# Revit family: Hager-Golf-IP40-Plain_Door-syst-CH-fr
name_source: partatom
category: Electrical Equipment
units: mm (PartAtom-declared; Revit-internal decimal feet)

## family parameters
Cut with Voids When Loaded = No
Host = Face
Panel Configuration = Two Columns, Circuits Across
Part Type = Panelboard
Room Calculation Point = No
Round Connector Dimension = Use Diameter
Shared = No

## types (22) — shared parameters
EF000007 - couleur = EV000202 - blanc
EF000116 - numéro RAL = 9010
EF000118 - avec cadre/support de montage = No
EF000339 - type de capot = EV004216 - porte
EF001062 - finition CEM = No
EF001088 - possibilité de montage en saillie = Yes
EF001596 - matériau du boîtier/corps = EV000139 - plastique
EF004462 - type de fermeture = EV000154 - autre
EF006244 - couvercle/porte transparent(e) = No
EF006306 - avec serrure = No
EF009212 - finition du couvercle = EV000116 - fermé
EF015941 - porte pour transmission du signal = Yes
HG000001 - nombre de colonnes = 1
HG000002 - avec porte = Yes
HG000003 - Gamme = Golf
HG000005 - Epaisseur = 3 mm  [stored 0.00984252 ft]
HG000009 - Porte à double battant = No
HG000010 - Portes asymétriques = No
HG000011 - Rangées du bas vides = No
HG000017 - Distance entre pôles = 18 mm  [stored 0.0590551 ft]
Manufacturer = Hager
Type Comments = Golf
zero-valued in all types: Default Elevation, HG000007 - Nombre de colonnes vides, HG000008 - Nombre de rangées vides

## per-type parameters (varying)
| type | EF000003 - mode de pose | EF000008 - largeur | EF000040 - hauteur | EF000049 - profondeur | EF000218 - profondeur d'encastrement | EF000266 - nombre de rangées | EF000332 - hauteur d'encastrement | EF000846 - largeur d'encastrement | EF001131 - profondeur intérieure | EF001134 - rail DIN | EF002950 - largeur en nombre de modules | EF005474 - indice de protection (IP) | EF015776 - borne de mise à la terre | EF015777 - borne à conducteur neutre | HG000004 - Référence fabricant | HG000006 - Encastré | Model |
| Encastré  L204 H225 P97.5 4 Modules - VF104PS | EV000383 - encastré | 204 mm | 225 mm  [stored 0.738189 ft] | 98 mm  [stored 0.321522 ft] | 72 mm  [stored 0.23622 ft] | 1 | 189 mm  [stored 0.620079 ft] | 170 mm  [stored 0.557743 ft] | 98 mm  [stored 0.321522 ft] | Yes | 4 |  | No | No | VF104PS | Yes | VF104PS |
| Encastré  L275 H225 P97.5 8 Modules - VF108PS | EV000383 - encastré | 275 mm | 225 mm  [stored 0.738189 ft] | 98 mm  [stored 0.321522 ft] | 72 mm  [stored 0.23622 ft] | 1 | 189 mm  [stored 0.620079 ft] | 242 mm  [stored 0.793963 ft] | 98 mm  [stored 0.321522 ft] | Yes | 8 |  | No | No | VF108PS | Yes | VF108PS |
| Encastré IP40 L352 H293 P97.5 12 Modules - VF112PS | EV000383 - encastré | 352 mm  [stored 1.15486 ft] | 293 mm | 98 mm  [stored 0.321522 ft] | 72 mm  [stored 0.23622 ft] | 1 | 257 mm  [stored 0.843176 ft] | 318 mm  [stored 1.04331 ft] | 98 mm  [stored 0.321522 ft] | Yes | 12 | EV006415 - IP40 | Yes | Yes | VF112PS | Yes | VF112PS |
| Encastré IP40 L352 H543 P97.5 12 Modules - VF312PS | EV000383 - encastré | 352 mm  [stored 1.15486 ft] | 543 mm  [stored 1.7815 ft] | 98 mm  [stored 0.321522 ft] | 72 mm  [stored 0.23622 ft] | 3 | 507 mm  [stored 1.66339 ft] | 318 mm  [stored 1.04331 ft] | 98 mm  [stored 0.321522 ft] | Yes | 12 | EV006415 - IP40 | Yes | Yes | VF312PS | Yes | VF312PS |
| Encastré IP40 L352 H688 P97.5 12 Modules - VF412PS | EV000383 - encastré | 352 mm  [stored 1.15486 ft] | 688 mm  [stored 2.25722 ft] | 98 mm  [stored 0.321522 ft] | 72 mm  [stored 0.23622 ft] | 4 | 652 mm  [stored 2.13911 ft] | 318 mm  [stored 1.04331 ft] | 98 mm  [stored 0.321522 ft] | Yes | 12 | EV006415 - IP40 | Yes | Yes | VF412PS | Yes | VF412PS |
| Encastré IP40 L382 H418 P97.5 12 Modules - VF212PS | EV000383 - encastré | 382 mm  [stored 1.25328 ft] | 418 mm  [stored 1.37139 ft] | 98 mm  [stored 0.321522 ft] | 72 mm  [stored 0.23622 ft] | 2 | 382 mm  [stored 1.25328 ft] | 318 mm  [stored 1.04331 ft] | 98 mm  [stored 0.321522 ft] | Yes | 12 | EV006415 - IP40 | Yes | Yes | VF212PS | Yes | VF212PS |
| Encastré IP40 L460 H293 P97.5 18 Modules - VF118PS | EV000383 - encastré | 460 mm  [stored 1.50919 ft] | 293 mm | 98 mm  [stored 0.321522 ft] | 72 mm  [stored 0.23622 ft] | 1 | 257 mm  [stored 0.843176 ft] | 426 mm  [stored 1.39764 ft] | 98 mm  [stored 0.321522 ft] | Yes | 18 | EV006415 - IP40 | Yes | Yes | VF118PS | Yes | VF118PS |
| Encastré IP40 L460 H418 P97.5 18 Modules - VF218PS | EV000383 - encastré | 460 mm  [stored 1.50919 ft] | 418 mm  [stored 1.37139 ft] | 98 mm  [stored 0.321522 ft] | 72 mm  [stored 0.23622 ft] | 2 | 382 mm  [stored 1.25328 ft] | 426 mm  [stored 1.39764 ft] | 98 mm  [stored 0.321522 ft] | Yes | 18 | EV006415 - IP40 | Yes | Yes | VF218PS | Yes | VF218PS |
| Encastré IP40 L460 H543 P97.5 18 Modules - VF318PS | EV000383 - encastré | 460 mm  [stored 1.50919 ft] | 543 mm  [stored 1.7815 ft] | 98 mm  [stored 0.321522 ft] | 72 mm  [stored 0.23622 ft] | 3 | 507 mm  [stored 1.66339 ft] | 426 mm  [stored 1.39764 ft] | 98 mm  [stored 0.321522 ft] | Yes | 18 | EV006415 - IP40 | Yes | Yes | VF318PS | Yes | VF318PS |
| Encastré IP40 L460 H688 P97.5 18 Modules - VF418PS | EV000383 - encastré | 460 mm  [stored 1.50919 ft] | 688 mm  [stored 2.25722 ft] | 98 mm  [stored 0.321522 ft] | 72 mm  [stored 0.23622 ft] | 4 | 652 mm  [stored 2.13911 ft] | 426 mm  [stored 1.39764 ft] | 98 mm  [stored 0.321522 ft] | Yes | 18 | EV006415 - IP40 | Yes | Yes | VF418PS | Yes | VF418PS |
| Encastré IP40 L532 H293 P97.5 22 Modules - VF122PS | EV000383 - encastré | 532 mm  [stored 1.74541 ft] | 293 mm | 98 mm  [stored 0.321522 ft] | 72 mm  [stored 0.23622 ft] | 1 | 257 mm  [stored 0.843176 ft] | 498 mm  [stored 1.63386 ft] | 98 mm  [stored 0.321522 ft] | Yes | 22 | EV006415 - IP40 | Yes | Yes | VF122PS | Yes | VF122PS |
| Saillie  L138 H184 P99 4 Modules - VS104PS | EV000384 - saillie | 138 mm  [stored 0.452756 ft] | 184 mm  [stored 0.603675 ft] | 99 mm  [stored 0.324803 ft] | 0 mm  [stored 0 ft] | 1 | 0 mm  [stored 0 ft] | 0 mm  [stored 0 ft] | 99 mm  [stored 0.324803 ft] | Yes | 4 |  | No | No | VS104PS | No | VS104PS |
| Saillie  L210 H184 P99 8 Modules - VS108PS | EV000384 - saillie | 210 mm  [stored 0.688976 ft] | 184 mm  [stored 0.603675 ft] | 99 mm  [stored 0.324803 ft] | 0 mm  [stored 0 ft] | 1 | 0 mm  [stored 0 ft] | 0 mm  [stored 0 ft] | 99 mm  [stored 0.324803 ft] | No | 8 |  | No | No | VS108PS | No | VS108PS |
| Saillie IP40 L282 H252 P99 12 Modules - VS112PS | EV000384 - saillie | 282 mm | 252 mm  [stored 0.826772 ft] | 99 mm  [stored 0.324803 ft] | 0 mm  [stored 0 ft] | 1 | 0 mm  [stored 0 ft] | 0 mm  [stored 0 ft] | 99 mm  [stored 0.324803 ft] | Yes | 12 | EV006415 - IP40 | Yes | Yes | VS112PS | No | VS112PS |
| Saillie IP40 L282 H377 P99 12 Modules - VS212PS | EV000384 - saillie | 282 mm | 377 mm  [stored 1.23688 ft] | 99 mm  [stored 0.324803 ft] | 0 mm  [stored 0 ft] | 2 | 0 mm  [stored 0 ft] | 0 mm  [stored 0 ft] | 99 mm  [stored 0.324803 ft] | Yes | 12 | EV006415 - IP40 | Yes | Yes | VS212PS | No | VS212PS |
| Saillie IP40 L282 H500 P99 12 Modules - VS312PS | EV000384 - saillie | 282 mm | 500 mm  [stored 1.64042 ft] | 99 mm  [stored 0.324803 ft] | 0 mm  [stored 0 ft] | 3 | 0 mm  [stored 0 ft] | 0 mm  [stored 0 ft] | 99 mm  [stored 0.324803 ft] | Yes | 12 | EV006415 - IP40 | Yes | Yes | VS312PS | No | VS312PS |
| Saillie IP40 L282 H647 P99 12 Modules - VS412PS | EV000384 - saillie | 282 mm | 647 mm  [stored 2.1227 ft] | 99 mm  [stored 0.324803 ft] | 0 mm  [stored 0 ft] | 4 | 0 mm  [stored 0 ft] | 0 mm  [stored 0 ft] | 99 mm  [stored 0.324803 ft] | Yes | 12 | EV006415 - IP40 | Yes | Yes | VS412PS | No | VS412PS |
| Saillie IP40 L390 H252 P99 18 Modules - VS118PS | EV000384 - saillie | 390 mm  [stored 1.27953 ft] | 252 mm  [stored 0.826772 ft] | 99 mm  [stored 0.324803 ft] | 0 mm  [stored 0 ft] | 1 | 0 mm  [stored 0 ft] | 0 mm  [stored 0 ft] | 99 mm  [stored 0.324803 ft] | Yes | 18 | EV006415 - IP40 | Yes | Yes | VS118PS | No | VS118PS |
| Saillie IP40 L390 H377 P99 18 Modules - VS218PS | EV000384 - saillie | 390 mm  [stored 1.27953 ft] | 377 mm  [stored 1.23688 ft] | 99 mm  [stored 0.324803 ft] | 0 mm  [stored 0 ft] | 2 | 0 mm  [stored 0 ft] | 0 mm  [stored 0 ft] | 99 mm  [stored 0.324803 ft] | Yes | 18 | EV006415 - IP40 | Yes | Yes | VS218PS | No | VS218PS |
| Saillie IP40 L390 H500 P99 18 Modules - VS318PS | EV000384 - saillie | 390 mm  [stored 1.27953 ft] | 500 mm  [stored 1.64042 ft] | 99 mm  [stored 0.324803 ft] | 0 mm  [stored 0 ft] | 3 | 0 mm  [stored 0 ft] | 0 mm  [stored 0 ft] | 99 mm  [stored 0.324803 ft] | Yes | 18 | EV006415 - IP40 | Yes | Yes | VS318PS | No | VS318PS |
| Saillie IP40 L390 H647 P99 18 Modules - VS418PS | EV000384 - saillie | 390 mm  [stored 1.27953 ft] | 647 mm  [stored 2.1227 ft] | 99 mm  [stored 0.324803 ft] | 0 mm  [stored 0 ft] | 4 | 0 mm  [stored 0 ft] | 0 mm  [stored 0 ft] | 99 mm  [stored 0.324803 ft] | Yes | 18 | EV006415 - IP40 | Yes | Yes | VS418PS | No | VS418PS |
| Saillie IP40 L462 H252 P99 22 Modules - VS122PS | EV000384 - saillie | 462 mm  [stored 1.51575 ft] | 252 mm  [stored 0.826772 ft] | 99 mm  [stored 0.324803 ft] | 0 mm  [stored 0 ft] | 1 | 0 mm  [stored 0 ft] | 0 mm  [stored 0 ft] | 99 mm  [stored 0.324803 ft] | Yes | 22 | EV006415 - IP40 | Yes | Yes | VS122PS | No | VS122PS |

note: [stored X ft] marks values corroborated as IEEE doubles in the binary element streams (Revit-internal decimal feet)

## geometry (parser evidence)
native form markers: Sweep x17
no freeform markers — native parametric forms only
